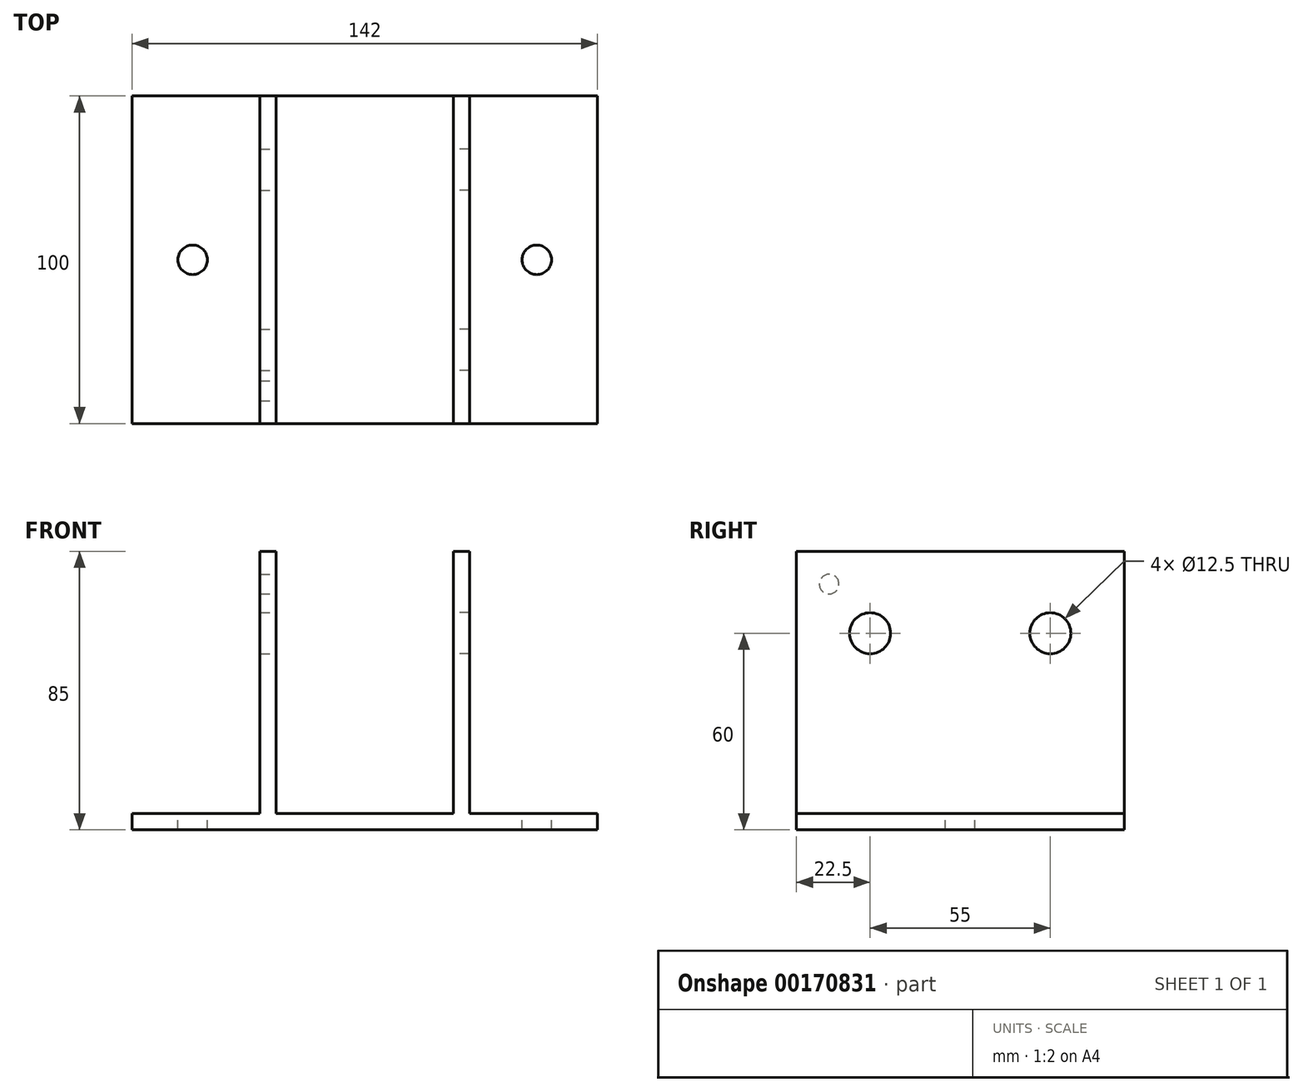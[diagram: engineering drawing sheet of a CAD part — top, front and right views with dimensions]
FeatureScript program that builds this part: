
annotation { "Feature Type Name" : "Feature", "Feature Type Description" : "" }
export const myFeature = defineFeature(function(context is Context, id is Id, definition is map)
    precondition{}
    {
        {
            var Q0;
            Q0=qCreatedBy(makeId("Top.planeOp"),FACE);
            var sketch = newSketch(context, id + "F0", { "sketchPlane" : qUnion([Q0])});
            skLineSegment(sketch, "E0.bottom", {"start": v(0, -50) * mm, "end": v(71, -50) * mm});
            skLineSegment(sketch, "E0.top", {"start": v(0, 50) * mm, "end": v(71, 50) * mm});
            skLineSegment(sketch, "E0.left", {"start": v(0, -50) * mm, "end": v(0, 50) * mm});
            skLineSegment(sketch, "E0.right", {"start": v(71, -50) * mm, "end": v(71, 50) * mm});
            skCircle(sketch, "E1", {"center": v(52.5, 0) * mm, "radius": 4.5 * mm});
            skSolve(sketch);
        }
        {
            var Q0;
            Q0 = qSketchRegion(id + "F0", true);
            extrude(context, id + "F1", {"entities" : qUnion([Q0]), "oppositeDirection" : true, "depth" : 5 * mm});
        }
        {
            var Q0;
            Q0=makeQuery(id+"F1.opExtrude","CAP_FACE",FACE,{"disambiguationData":[OSD([sQuery(id+"F0.wireOp",EDGE,"E0.bottom"),sQuery(id+"F0.wireOp",EDGE,"E0.top"),sQuery(id+"F0.wireOp",EDGE,"E0.left"),sQuery(id+"F0.wireOp",EDGE,"E0.right")])],"isStart":true});
            var sketch = newSketch(context, id + "F2", { "sketchPlane" : qUnion([Q0])});
            skLineSegment(sketch, "E2.bottom", {"start": v(27, 50) * mm, "end": v(32, 50) * mm});
            skLineSegment(sketch, "E2.top", {"start": v(27, -50) * mm, "end": v(32, -50) * mm});
            skLineSegment(sketch, "E2.left", {"start": v(27, 50) * mm, "end": v(27, -50) * mm});
            skLineSegment(sketch, "E2.right", {"start": v(32, 50) * mm, "end": v(32, -50) * mm});
            skSolve(sketch);
        }
        {
            var Q0;
            Q0 = qSketchRegion(id + "F2", true);
            extrude(context, id + "F3", {"entities" : qUnion([Q0]), "operationType" : NewBodyOperationType.ADD, "depth" : 80 * mm});
        }
        {
            var Q0;
            Q0=qCreatedBy(makeId("Right.planeOp"),FACE);
            var sketch = newSketch(context, id + "F4", { "sketchPlane" : qUnion([Q0])});
            skCircle(sketch, "E3", {"center": v(-27.5, 55) * mm, "radius": 6.25 * mm});
            skLineSegment(sketch, "E4", {"start": v(-27.5, 55) * mm, "end": v(27.5, 55) * mm, "construction": true});
            skCircle(sketch, "E5", {"center": v(27.5, 55) * mm, "radius": 6.25 * mm});
            skLineSegment(sketch, "E6", {"start": v(0, 0) * mm, "end": v(0, 55) * mm, "construction": true});
            skSolve(sketch);
        }
        {
            var Q0;
            Q0=makeQuery(id+"F4.imprint","IMPRINT",FACE,{"disambiguationData":[TD([[makeQuery(id+"F4.imprint","IMPRINT",EDGE,{"derivedFrom":sQuery(id+"F4.wireOp",EDGE,"E3")}),1.0]])]});
            var Q1;
            Q1=makeQuery(id+"F4.imprint","IMPRINT",FACE,{"disambiguationData":[TD([[makeQuery(id+"F4.imprint","IMPRINT",EDGE,{"derivedFrom":sQuery(id+"F4.wireOp",EDGE,"E5")}),1.0]])]});
            extrude(context, id + "F5", {"entities" : qUnion([Q0, Q1]), "operationType" : NewBodyOperationType.REMOVE, "endBound" : BoundingType.THROUGH_ALL, "depth" : 25 * mm});
        }
        {
            var Q0;
            Q0=makeQuery(id+"F1.opExtrude","SWEPT_BODY",BODY,{"disambiguationData":[OSD([sQuery(id+"F0.wireOp",EDGE,"E0.bottom"),sQuery(id+"F0.wireOp",EDGE,"E0.top"),sQuery(id+"F0.wireOp",EDGE,"E0.left"),sQuery(id+"F0.wireOp",EDGE,"E0.right")])]});
            var Q1;
            Q1=makeQuery(id+"F1.opExtrude","SWEPT_FACE",FACE,{"disambiguationData":[OSD([sQuery(id+"F0.wireOp",EDGE,"E0.left")])]});
            mirror(context, id + "F6", {"operationType" : NewBodyOperationType.ADD, "entities" : qUnion([Q0]), "mirrorPlane" : qUnion([Q1])});
        }
        {
            var Q0;
            Q0=qCreatedBy(makeId("Right.planeOp"),FACE);
            var sketch = newSketch(context, id + "F7", { "sketchPlane" : qUnion([Q0])});
            skCircle(sketch, "E7", {"center": v(-40, 70) * mm, "radius": 3 * mm});
            skSolve(sketch);
        }
        {
            var Q0;
            Q0=makeQuery(id+"F7.imprint","IMPRINT",FACE,{"disambiguationData":[TD([[makeQuery(id+"F7.imprint","IMPRINT",EDGE,{"derivedFrom":sQuery(id+"F7.wireOp",EDGE,"E7")}),1.0]])]});
            extrude(context, id + "F8", {"entities" : qUnion([Q0]), "operationType" : NewBodyOperationType.REMOVE, "endBound" : BoundingType.THROUGH_ALL, "oppositeDirection" : true, "depth" : 25 * mm});
        }
    });
